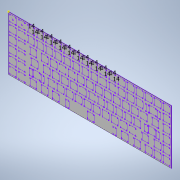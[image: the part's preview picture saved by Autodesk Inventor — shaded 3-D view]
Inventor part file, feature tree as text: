
AUTODESK INVENTOR PART (.ipt)
format: ipt  version: 2020 (Build 240168000, 168)  size: 543,232 bytes
history: native  units: mm
features: sheet_metal_op x1, sketch x1, other x1
ambient origin geometry x8: Origin, YZ Plane, XZ Plane, XY Plane, X Axis, Y Axis, Z Axis, Center Point
bodies: Body1 (feature_tree)
feature tree (3):
  sheet_metal_op  "Face2"
  sketch  "Sketch1"  dims[d15=0.5mm d16=14.0mm d17=14.0mm d18=14.0mm d19=14.0mm d20=14.0mm d21=14.0mm d22=14.0mm d23=14.0mm d24=14.0mm d25=14.0mm d26=14.0mm d27=14.0mm d28=14.0mm d29=14.0mm d30=14.0mm d31=14.0mm d32=14.0mm d33=14.0mm d34=14.0mm d35=14.0mm d9=0.5mm d10=0.872665mm d11=0.5mm d12=0.872665mm]
  other  "Plate2"
